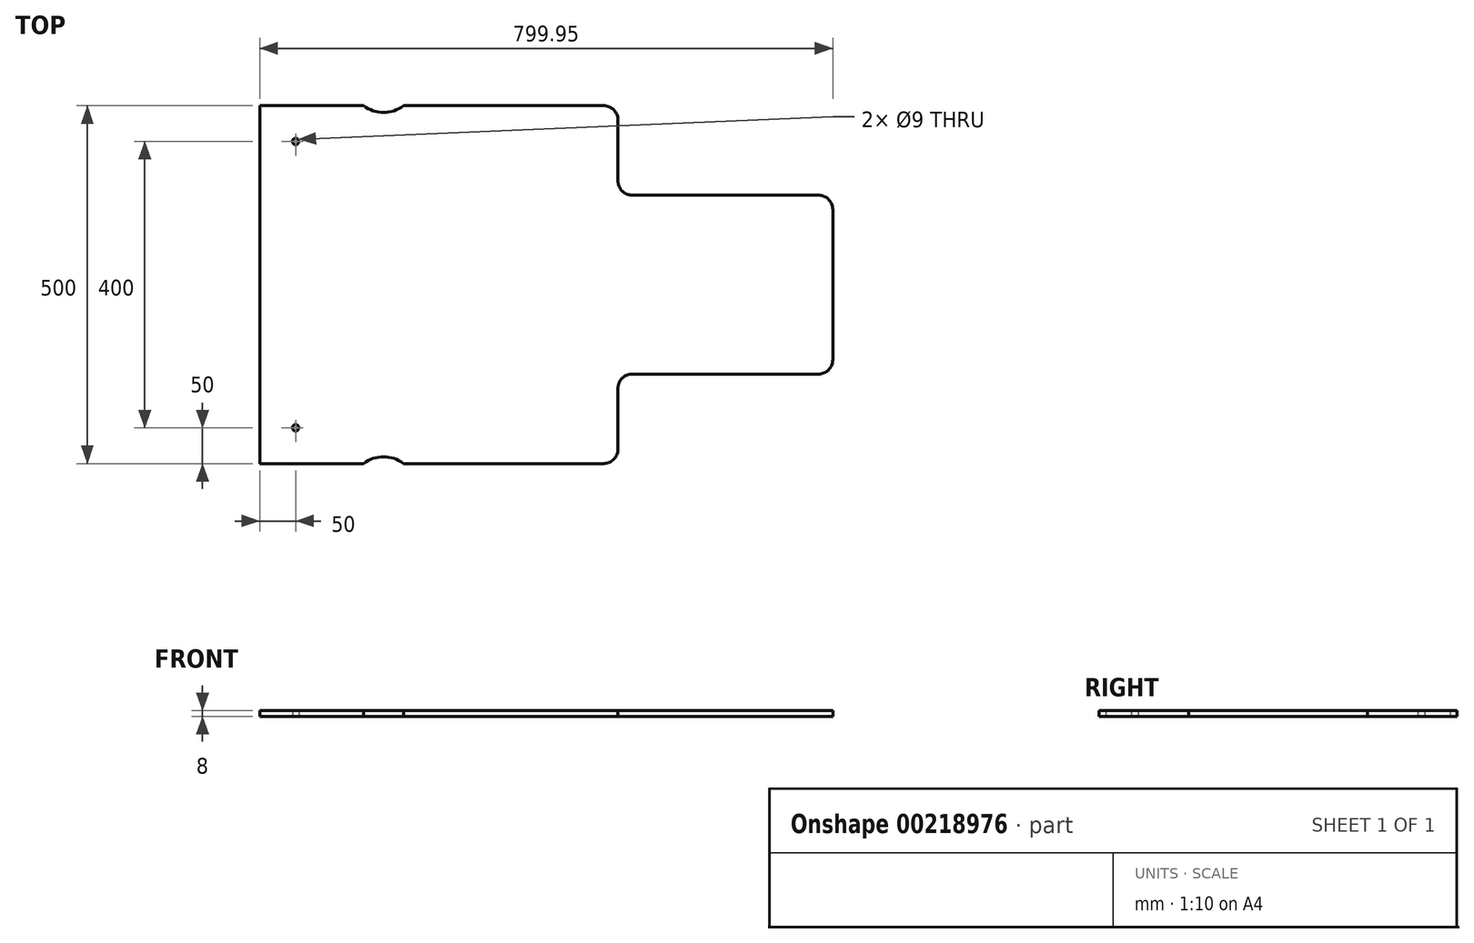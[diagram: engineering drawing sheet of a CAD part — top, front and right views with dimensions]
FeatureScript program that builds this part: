
annotation { "Feature Type Name" : "Feature", "Feature Type Description" : "" }
export const myFeature = defineFeature(function(context is Context, id is Id, definition is map)
    precondition{}
    {
        {
            var Q0;
            Q0=qCreatedBy(makeId("Top.planeOp"),FACE);
            var sketch = newSketch(context, id + "F0", { "sketchPlane" : qUnion([Q0])});
            skLineSegment(sketch, "E0", {"start": v(-19.95, 250) * mm, "end": v(-299.5, 250) * mm});
            skArc(sketch, "E1", {"start": v(-354.95, 250) * mm, "mid": v(-327.23, 240.45) * mm, "end": v(-299.5, 250) * mm});
            skLineSegment(sketch, "E2.trimOffspring", {"start": v(-354.95, 250) * mm, "end": v(-499.95, 250) * mm});
            skLineSegment(sketch, "E3", {"start": v(-559.95, 250) * mm, "end": v(-559.95, -250) * mm});
            skLineSegment(sketch, "E4", {"start": v(-559.95, 250) * mm, "end": v(-589.95, 250) * mm});
            skLineSegment(sketch, "E5", {"start": v(-609.95, 230) * mm, "end": v(-609.95, -230) * mm});
            skLineSegment(sketch, "E6", {"start": v(-589.95, -250) * mm, "end": v(-559.95, -250) * mm});
            skArc(sketch, "E7.MirrorCS", {"start": v(-354.95, -250) * mm, "mid": v(-327.23, -240.45) * mm, "end": v(-299.5, -250) * mm});
            skLineSegment(sketch, "E8.trimOffspring", {"start": v(-299.5, -250) * mm, "end": v(-19.95, -250) * mm});
            skLineSegment(sketch, "E9", {"start": v(-499.95, 250) * mm, "end": v(-499.95, -250) * mm});
            skLineSegment(sketch, "E10", {"start": v(-354.95, -250) * mm, "end": v(-499.95, -250) * mm});
            skPoint(sketch, "E11", {"position": v(-49.95, 200) * mm});
            skPoint(sketch, "E12.MirrorP", {"position": v(-49.95, -200) * mm});
            skPoint(sketch, "E13", {"position": v(-449.95, 200) * mm});
            skPoint(sketch, "E14.MirrorP", {"position": v(-449.95, -200) * mm});
            skPoint(sketch, "E15.visualSharp", {"position": v(-609.95, 250) * mm});
            skArc(sketch, "E15.filletArc", {"start": v(-589.95, 250) * mm, "mid": v(-604.1, 244.14) * mm, "end": v(-609.95, 230) * mm});
            skPoint(sketch, "E16.visualSharp", {"position": v(-609.95, -250) * mm});
            skArc(sketch, "E16.filletArc", {"start": v(-609.95, -230) * mm, "mid": v(-604.1, -244.14) * mm, "end": v(-589.95, -250) * mm});
            skPoint(sketch, "E17.visualSharp", {"position": v(0.05, -250) * mm});
            skArc(sketch, "E17.filletArc", {"start": v(-19.95, -250) * mm, "mid": v(-5.8, -244.14) * mm, "end": v(0.05, -230) * mm});
            skPoint(sketch, "E18.visualSharp", {"position": v(0.05, 250) * mm});
            skArc(sketch, "E18.filletArc", {"start": v(0.05, 230) * mm, "mid": v(-5.8, 244.14) * mm, "end": v(-19.95, 250) * mm});
            skLineSegment(sketch, "E19", {"start": v(-559.95, 250) * mm, "end": v(-499.95, 250) * mm});
            skLineSegment(sketch, "E20", {"start": v(-559.95, -250) * mm, "end": v(-499.95, -250) * mm});
            skLineSegment(sketch, "E21", {"start": v(20, 125) * mm, "end": v(280, 125) * mm});
            skLineSegment(sketch, "E22", {"start": v(300, 105) * mm, "end": v(300, -105) * mm});
            skLineSegment(sketch, "E23", {"start": v(280, -125) * mm, "end": v(20, -125) * mm});
            skLineSegment(sketch, "E24", {"start": v(0, -145) * mm, "end": v(0.05, -230) * mm});
            skLineSegment(sketch, "E25", {"start": v(0.05, 230) * mm, "end": v(0, 145) * mm});
            skPoint(sketch, "E26.visualSharp", {"position": v(300, 125) * mm});
            skArc(sketch, "E26.filletArc", {"start": v(300, 105) * mm, "mid": v(294.14, 119.14) * mm, "end": v(280, 125) * mm});
            skPoint(sketch, "E27.visualSharp", {"position": v(300, -125) * mm});
            skArc(sketch, "E27.filletArc", {"start": v(280, -125) * mm, "mid": v(294.14, -119.14) * mm, "end": v(300, -105) * mm});
            skPoint(sketch, "E28.visualSharp", {"position": v(0, -125) * mm});
            skArc(sketch, "E28.filletArc", {"start": v(20, -125) * mm, "mid": v(5.86, -130.86) * mm, "end": v(0, -145) * mm});
            skPoint(sketch, "E29.visualSharp", {"position": v(0, 125) * mm});
            skArc(sketch, "E29.filletArc", {"start": v(0, 145) * mm, "mid": v(5.86, 130.86) * mm, "end": v(20, 125) * mm});
            skSolve(sketch);
        }
        {
            var Q0;
            Q0=makeQuery(id+"F0.imprint","IMPRINT",FACE,{"disambiguationData":[TD([[makeQuery(id+"F0.imprint","IMPRINT",EDGE,{"derivedFrom":sQuery(id+"F0.wireOp",EDGE,"E3")}),-1.0]])]});
            cPlane(context, id + "F1", {"entities" : qUnion([Q0]), "cplaneType" : CPlaneType.OFFSET, "offset" : 50 * mm, "width" : 150 * mm, "height" : 150 * mm});
        }
        {
            var Q0;
            Q0=makeQuery(id+"F0.imprint","IMPRINT",FACE,{"disambiguationData":[TD([[makeQuery(id+"F0.imprint","IMPRINT",EDGE,{"derivedFrom":sQuery(id+"F0.wireOp",EDGE,"E0")}),1.0]])]});
            extrude(context, id + "F2", {"entities" : qUnion([Q0]), "depth" : 8 * mm, "offsetDistance" : 25 * mm});
        }
        {
            var Q0;
            Q0=sQuery(id+"F0.wireOp",VERTEX,"E14.MirrorP");
            var Q1;
            Q1=sQuery(id+"F0.wireOp",VERTEX,"E13");
            var Q2;
            Q2=makeQuery(id+"F2.opExtrude","SWEPT_BODY",BODY,{"disambiguationData":[OSD([sQuery(id+"F0.wireOp",EDGE,"E0"),sQuery(id+"F0.wireOp",EDGE,"E1"),sQuery(id+"F0.wireOp",EDGE,"E2.trimOffspring"),sQuery(id+"F0.wireOp",EDGE,"E7.MirrorCS"),sQuery(id+"F0.wireOp",EDGE,"E8.trimOffspring"),sQuery(id+"F0.wireOp",EDGE,"E9"),sQuery(id+"F0.wireOp",EDGE,"E10"),sQuery(id+"F0.wireOp",EDGE,"E17.filletArc"),sQuery(id+"F0.wireOp",EDGE,"E18.filletArc"),sQuery(id+"F0.wireOp",EDGE,"E21"),sQuery(id+"F0.wireOp",EDGE,"E22"),sQuery(id+"F0.wireOp",EDGE,"E23"),sQuery(id+"F0.wireOp",EDGE,"E24"),sQuery(id+"F0.wireOp",EDGE,"E25"),sQuery(id+"F0.wireOp",EDGE,"E26.filletArc"),sQuery(id+"F0.wireOp",EDGE,"E27.filletArc"),sQuery(id+"F0.wireOp",EDGE,"E28.filletArc"),sQuery(id+"F0.wireOp",EDGE,"E29.filletArc")])]});
            hole(context, id + "F3", {"style" : HoleStyle.SIMPLE, "endStyle" : HoleEndStyle.THROUGH, "oppositeDirection" : true, "standardTappedOrClearance" : lookupTablePath({ "fit" : "Normal", "standard" : "ISO", "size" : "M8", "type" : "Clearance" }), "standardBlindInLast" : lookupTablePath({ "fit" : "Normal", "standard" : "ISO", "engagement" : "75%", "pitch" : "1.25 mm", "size" : "M8", "type" : "Clearance & tapped" }), "holeDiameter" : 9 * mm, "majorDiameter" : 8 * mm, "isTappedThrough" : true, "tappedDepth" : 12 * mm, "tapClearance" : 3, "locations" : qUnion([Q0, Q1]), "scope" : qUnion([Q2])});
        }
    });
